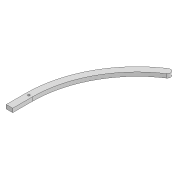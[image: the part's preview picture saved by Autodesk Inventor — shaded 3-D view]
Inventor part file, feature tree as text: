
AUTODESK INVENTOR PART (.ipt)
format: ipt  version: 2022 (Build 260153000, 153)  size: 90,624 bytes
history: native  units: mm
features: extrude x1, sketch x1
ambient origin geometry x8: Origin, YZ Plane, XZ Plane, XY Plane, X Axis, Y Axis, Z Axis, Center Point
bodies: Solid1 (feature_tree)
feature tree (2):
  extrude  "Extrusion1"  Depth=10.0mm
  sketch  "Sketch1"  dims[d0=10.0mm d1=10.0mm d3=30.0mm d4=10.0mm d6=170.0mm d7=70.0mm d8=3.3mm d9=6.0mm d10=0.0mm]
